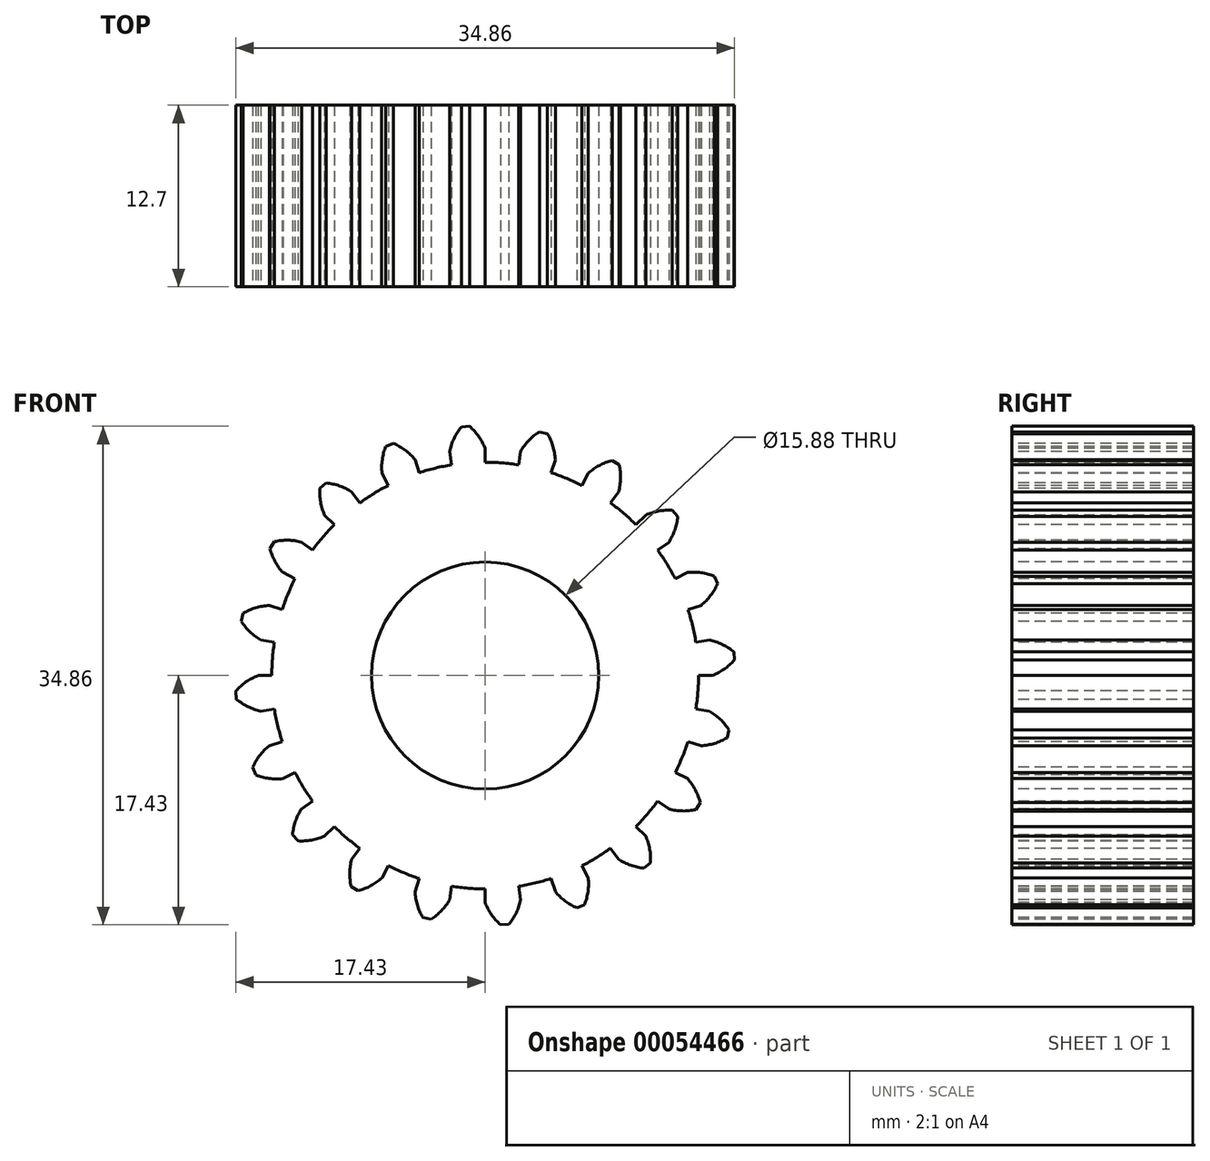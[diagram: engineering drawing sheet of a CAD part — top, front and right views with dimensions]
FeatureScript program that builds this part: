
annotation { "Feature Type Name" : "Feature", "Feature Type Description" : "" }
export const myFeature = defineFeature(function(context is Context, id is Id, definition is map)
    precondition{}
    {
        {
            var Q0;
            Q0=qCreatedBy(makeId("Front.planeOp"),FACE);
            var sketch = newSketch(context, id + "F0", { "sketchPlane" : qUnion([Q0])});
            skArc(sketch, "E0", {"start": v(2.33, 14.73) * mm, "mid": v(1.17, 14.87) * mm, "end": v(0, 14.92) * mm});
            skArc(sketch, "E1", {"start": v(0, 15.88) * mm, "mid": v(-0.45, 16.72) * mm, "end": v(-1.08, 17.43) * mm});
            skLineSegment(sketch, "E2", {"start": v(0, 15.88) * mm, "end": v(0, 14.92) * mm});
            skLineSegment(sketch, "E3.MirrorCS", {"start": v(-2.48, 15.68) * mm, "end": v(-2.33, 14.73) * mm});
            skArc(sketch, "E4.MirrorCS", {"start": v(-2.48, 15.68) * mm, "mid": v(-2.17, 16.58) * mm, "end": v(-1.66, 17.38) * mm});
            skLineSegment(sketch, "E5", {"start": v(-1.66, 17.38) * mm, "end": v(-1.08, 17.43) * mm});
            skLineSegment(sketch, "E6.1.0", {"start": v(-4.9, 15.1) * mm, "end": v(-4.6, 14.19) * mm});
            skArc(sketch, "E6.1.1", {"start": v(-4.9, 15.1) * mm, "mid": v(-5.6, 15.76) * mm, "end": v(-6.41, 16.24) * mm});
            skLineSegment(sketch, "E6.1.2", {"start": v(-6.95, 16.02) * mm, "end": v(-6.41, 16.24) * mm});
            skArc(sketch, "E6.1.3", {"start": v(-7.2, 14.14) * mm, "mid": v(-7.2, 15.1) * mm, "end": v(-6.95, 16.02) * mm});
            skLineSegment(sketch, "E6.1.4", {"start": v(-7.2, 14.14) * mm, "end": v(-6.77, 13.3) * mm});
            skLineSegment(sketch, "E6.2.0", {"start": v(-9.33, 12.84) * mm, "end": v(-8.77, 12.07) * mm});
            skArc(sketch, "E6.2.1", {"start": v(-9.33, 12.84) * mm, "mid": v(-10.19, 13.26) * mm, "end": v(-11.12, 13.46) * mm});
            skLineSegment(sketch, "E6.2.2", {"start": v(-11.56, 13.09) * mm, "end": v(-11.12, 13.46) * mm});
            skArc(sketch, "E6.2.3", {"start": v(-11.23, 11.23) * mm, "mid": v(-11.5, 12.14) * mm, "end": v(-11.56, 13.09) * mm});
            skLineSegment(sketch, "E6.2.4", {"start": v(-11.23, 11.23) * mm, "end": v(-10.55, 10.55) * mm});
            skLineSegment(sketch, "E6.3.0", {"start": v(-12.84, 9.33) * mm, "end": v(-12.07, 8.77) * mm});
            skArc(sketch, "E6.3.1", {"start": v(-12.84, 9.33) * mm, "mid": v(-13.79, 9.46) * mm, "end": v(-14.74, 9.37) * mm});
            skLineSegment(sketch, "E6.3.2", {"start": v(-15.04, 8.88) * mm, "end": v(-14.74, 9.37) * mm});
            skArc(sketch, "E6.3.3", {"start": v(-14.14, 7.2) * mm, "mid": v(-14.7, 7.99) * mm, "end": v(-15.04, 8.88) * mm});
            skLineSegment(sketch, "E6.3.4", {"start": v(-14.14, 7.2) * mm, "end": v(-13.3, 6.77) * mm});
            skLineSegment(sketch, "E6.4.0", {"start": v(-15.1, 4.9) * mm, "end": v(-14.19, 4.6) * mm});
            skArc(sketch, "E6.4.1", {"start": v(-15.1, 4.9) * mm, "mid": v(-16.04, 4.74) * mm, "end": v(-16.91, 4.36) * mm});
            skLineSegment(sketch, "E6.4.2", {"start": v(-17.05, 3.8) * mm, "end": v(-16.91, 4.36) * mm});
            skArc(sketch, "E6.4.3", {"start": v(-15.68, 2.48) * mm, "mid": v(-16.44, 3.06) * mm, "end": v(-17.05, 3.8) * mm});
            skLineSegment(sketch, "E6.4.4", {"start": v(-15.68, 2.48) * mm, "end": v(-14.73, 2.33) * mm});
            skLineSegment(sketch, "E6.5.0", {"start": v(-15.88, 0) * mm, "end": v(-14.92, 0) * mm});
            skArc(sketch, "E6.5.1", {"start": v(-15.88, 0) * mm, "mid": v(-16.72, -0.45) * mm, "end": v(-17.43, -1.08) * mm});
            skLineSegment(sketch, "E6.5.2", {"start": v(-17.38, -1.66) * mm, "end": v(-17.43, -1.08) * mm});
            skArc(sketch, "E6.5.3", {"start": v(-15.68, -2.48) * mm, "mid": v(-16.58, -2.17) * mm, "end": v(-17.38, -1.66) * mm});
            skLineSegment(sketch, "E6.5.4", {"start": v(-15.68, -2.48) * mm, "end": v(-14.73, -2.33) * mm});
            skLineSegment(sketch, "E6.6.0", {"start": v(-15.1, -4.9) * mm, "end": v(-14.19, -4.6) * mm});
            skArc(sketch, "E6.6.1", {"start": v(-15.1, -4.9) * mm, "mid": v(-15.76, -5.6) * mm, "end": v(-16.24, -6.41) * mm});
            skLineSegment(sketch, "E6.6.2", {"start": v(-16.02, -6.95) * mm, "end": v(-16.24, -6.41) * mm});
            skArc(sketch, "E6.6.3", {"start": v(-14.14, -7.2) * mm, "mid": v(-15.1, -7.2) * mm, "end": v(-16.02, -6.95) * mm});
            skLineSegment(sketch, "E6.6.4", {"start": v(-14.14, -7.2) * mm, "end": v(-13.3, -6.77) * mm});
            skLineSegment(sketch, "E6.7.0", {"start": v(-12.84, -9.33) * mm, "end": v(-12.07, -8.77) * mm});
            skArc(sketch, "E6.7.1", {"start": v(-12.84, -9.33) * mm, "mid": v(-13.26, -10.19) * mm, "end": v(-13.46, -11.12) * mm});
            skLineSegment(sketch, "E6.7.2", {"start": v(-13.09, -11.56) * mm, "end": v(-13.46, -11.12) * mm});
            skArc(sketch, "E6.7.3", {"start": v(-11.23, -11.23) * mm, "mid": v(-12.14, -11.5) * mm, "end": v(-13.09, -11.56) * mm});
            skLineSegment(sketch, "E6.7.4", {"start": v(-11.23, -11.23) * mm, "end": v(-10.55, -10.55) * mm});
            skLineSegment(sketch, "E6.8.0", {"start": v(-9.33, -12.84) * mm, "end": v(-8.77, -12.07) * mm});
            skArc(sketch, "E6.8.1", {"start": v(-9.33, -12.84) * mm, "mid": v(-9.46, -13.79) * mm, "end": v(-9.37, -14.74) * mm});
            skLineSegment(sketch, "E6.8.2", {"start": v(-8.88, -15.04) * mm, "end": v(-9.37, -14.74) * mm});
            skArc(sketch, "E6.8.3", {"start": v(-7.2, -14.14) * mm, "mid": v(-7.99, -14.7) * mm, "end": v(-8.88, -15.04) * mm});
            skLineSegment(sketch, "E6.8.4", {"start": v(-7.2, -14.14) * mm, "end": v(-6.77, -13.3) * mm});
            skLineSegment(sketch, "E6.9.0", {"start": v(-4.9, -15.1) * mm, "end": v(-4.6, -14.19) * mm});
            skArc(sketch, "E6.9.1", {"start": v(-4.9, -15.1) * mm, "mid": v(-4.74, -16.04) * mm, "end": v(-4.36, -16.91) * mm});
            skLineSegment(sketch, "E6.9.2", {"start": v(-3.8, -17.05) * mm, "end": v(-4.36, -16.91) * mm});
            skArc(sketch, "E6.9.3", {"start": v(-2.48, -15.68) * mm, "mid": v(-3.06, -16.44) * mm, "end": v(-3.8, -17.05) * mm});
            skLineSegment(sketch, "E6.9.4", {"start": v(-2.48, -15.68) * mm, "end": v(-2.33, -14.73) * mm});
            skLineSegment(sketch, "E6.10.0", {"start": v(0, -15.88) * mm, "end": v(0, -14.92) * mm});
            skArc(sketch, "E6.10.1", {"start": v(0, -15.88) * mm, "mid": v(0.45, -16.72) * mm, "end": v(1.08, -17.43) * mm});
            skLineSegment(sketch, "E6.10.2", {"start": v(1.66, -17.38) * mm, "end": v(1.08, -17.43) * mm});
            skArc(sketch, "E6.10.3", {"start": v(2.48, -15.68) * mm, "mid": v(2.17, -16.58) * mm, "end": v(1.66, -17.38) * mm});
            skLineSegment(sketch, "E6.10.4", {"start": v(2.48, -15.68) * mm, "end": v(2.33, -14.73) * mm});
            skLineSegment(sketch, "E6.11.0", {"start": v(4.9, -15.1) * mm, "end": v(4.6, -14.19) * mm});
            skArc(sketch, "E6.11.1", {"start": v(4.9, -15.1) * mm, "mid": v(5.6, -15.76) * mm, "end": v(6.41, -16.24) * mm});
            skLineSegment(sketch, "E6.11.2", {"start": v(6.95, -16.02) * mm, "end": v(6.41, -16.24) * mm});
            skArc(sketch, "E6.11.3", {"start": v(7.2, -14.14) * mm, "mid": v(7.2, -15.1) * mm, "end": v(6.95, -16.02) * mm});
            skLineSegment(sketch, "E6.11.4", {"start": v(7.2, -14.14) * mm, "end": v(6.77, -13.3) * mm});
            skLineSegment(sketch, "E6.12.0", {"start": v(9.33, -12.84) * mm, "end": v(8.77, -12.07) * mm});
            skArc(sketch, "E6.12.1", {"start": v(9.33, -12.84) * mm, "mid": v(10.19, -13.26) * mm, "end": v(11.12, -13.46) * mm});
            skLineSegment(sketch, "E6.12.2", {"start": v(11.56, -13.09) * mm, "end": v(11.12, -13.46) * mm});
            skArc(sketch, "E6.12.3", {"start": v(11.23, -11.23) * mm, "mid": v(11.5, -12.14) * mm, "end": v(11.56, -13.09) * mm});
            skLineSegment(sketch, "E6.12.4", {"start": v(11.23, -11.23) * mm, "end": v(10.55, -10.55) * mm});
            skLineSegment(sketch, "E6.13.0", {"start": v(12.84, -9.33) * mm, "end": v(12.07, -8.77) * mm});
            skArc(sketch, "E6.13.1", {"start": v(12.84, -9.33) * mm, "mid": v(13.79, -9.46) * mm, "end": v(14.74, -9.37) * mm});
            skLineSegment(sketch, "E6.13.2", {"start": v(15.04, -8.88) * mm, "end": v(14.74, -9.37) * mm});
            skArc(sketch, "E6.13.3", {"start": v(14.14, -7.2) * mm, "mid": v(14.7, -7.99) * mm, "end": v(15.04, -8.88) * mm});
            skLineSegment(sketch, "E6.13.4", {"start": v(14.14, -7.2) * mm, "end": v(13.3, -6.77) * mm});
            skLineSegment(sketch, "E6.14.0", {"start": v(15.1, -4.9) * mm, "end": v(14.19, -4.6) * mm});
            skArc(sketch, "E6.14.1", {"start": v(15.1, -4.9) * mm, "mid": v(16.04, -4.74) * mm, "end": v(16.91, -4.36) * mm});
            skLineSegment(sketch, "E6.14.2", {"start": v(17.05, -3.8) * mm, "end": v(16.91, -4.36) * mm});
            skArc(sketch, "E6.14.3", {"start": v(15.68, -2.48) * mm, "mid": v(16.44, -3.06) * mm, "end": v(17.05, -3.8) * mm});
            skLineSegment(sketch, "E6.14.4", {"start": v(15.68, -2.48) * mm, "end": v(14.73, -2.33) * mm});
            skLineSegment(sketch, "E6.15.0", {"start": v(15.88, 0) * mm, "end": v(14.92, 0) * mm});
            skArc(sketch, "E6.15.1", {"start": v(15.88, 0) * mm, "mid": v(16.72, 0.45) * mm, "end": v(17.43, 1.08) * mm});
            skLineSegment(sketch, "E6.15.2", {"start": v(17.38, 1.66) * mm, "end": v(17.43, 1.08) * mm});
            skArc(sketch, "E6.15.3", {"start": v(15.68, 2.48) * mm, "mid": v(16.58, 2.17) * mm, "end": v(17.38, 1.66) * mm});
            skLineSegment(sketch, "E6.15.4", {"start": v(15.68, 2.48) * mm, "end": v(14.73, 2.33) * mm});
            skLineSegment(sketch, "E6.16.0", {"start": v(15.1, 4.9) * mm, "end": v(14.19, 4.6) * mm});
            skArc(sketch, "E6.16.1", {"start": v(15.1, 4.9) * mm, "mid": v(15.76, 5.6) * mm, "end": v(16.24, 6.41) * mm});
            skLineSegment(sketch, "E6.16.2", {"start": v(16.02, 6.95) * mm, "end": v(16.24, 6.41) * mm});
            skArc(sketch, "E6.16.3", {"start": v(14.14, 7.2) * mm, "mid": v(15.1, 7.2) * mm, "end": v(16.02, 6.95) * mm});
            skLineSegment(sketch, "E6.16.4", {"start": v(14.14, 7.2) * mm, "end": v(13.3, 6.77) * mm});
            skLineSegment(sketch, "E6.17.0", {"start": v(12.84, 9.33) * mm, "end": v(12.07, 8.77) * mm});
            skArc(sketch, "E6.17.1", {"start": v(12.84, 9.33) * mm, "mid": v(13.26, 10.19) * mm, "end": v(13.46, 11.12) * mm});
            skLineSegment(sketch, "E6.17.2", {"start": v(13.09, 11.56) * mm, "end": v(13.46, 11.12) * mm});
            skArc(sketch, "E6.17.3", {"start": v(11.23, 11.23) * mm, "mid": v(12.14, 11.5) * mm, "end": v(13.09, 11.56) * mm});
            skLineSegment(sketch, "E6.17.4", {"start": v(11.23, 11.23) * mm, "end": v(10.55, 10.55) * mm});
            skLineSegment(sketch, "E6.18.0", {"start": v(9.33, 12.84) * mm, "end": v(8.77, 12.07) * mm});
            skArc(sketch, "E6.18.1", {"start": v(9.33, 12.84) * mm, "mid": v(9.46, 13.79) * mm, "end": v(9.37, 14.74) * mm});
            skLineSegment(sketch, "E6.18.2", {"start": v(8.88, 15.04) * mm, "end": v(9.37, 14.74) * mm});
            skArc(sketch, "E6.18.3", {"start": v(7.2, 14.14) * mm, "mid": v(7.99, 14.7) * mm, "end": v(8.88, 15.04) * mm});
            skLineSegment(sketch, "E6.18.4", {"start": v(7.2, 14.14) * mm, "end": v(6.77, 13.3) * mm});
            skLineSegment(sketch, "E6.19.0", {"start": v(4.9, 15.1) * mm, "end": v(4.6, 14.19) * mm});
            skArc(sketch, "E6.19.1", {"start": v(4.9, 15.1) * mm, "mid": v(4.74, 16.04) * mm, "end": v(4.36, 16.91) * mm});
            skLineSegment(sketch, "E6.19.2", {"start": v(3.8, 17.05) * mm, "end": v(4.36, 16.91) * mm});
            skArc(sketch, "E6.19.3", {"start": v(2.48, 15.68) * mm, "mid": v(3.06, 16.44) * mm, "end": v(3.8, 17.05) * mm});
            skLineSegment(sketch, "E6.19.4", {"start": v(2.48, 15.68) * mm, "end": v(2.33, 14.73) * mm});
            skArc(sketch, "E7.trimOffspring", {"start": v(6.77, 13.3) * mm, "mid": v(5.7, 13.78) * mm, "end": v(4.6, 14.19) * mm});
            skArc(sketch, "E8.trimOffspring", {"start": v(10.55, 10.55) * mm, "mid": v(9.69, 11.34) * mm, "end": v(8.77, 12.07) * mm});
            skArc(sketch, "E9.trimOffspring", {"start": v(13.3, 6.77) * mm, "mid": v(12.72, 7.8) * mm, "end": v(12.07, 8.77) * mm});
            skArc(sketch, "E10.trimOffspring", {"start": v(14.73, 2.33) * mm, "mid": v(14.5, 3.48) * mm, "end": v(14.19, 4.6) * mm});
            skArc(sketch, "E11.trimOffspring", {"start": v(14.73, -2.33) * mm, "mid": v(14.87, -1.17) * mm, "end": v(14.92, 0) * mm});
            skArc(sketch, "E12.trimOffspring", {"start": v(13.3, -6.77) * mm, "mid": v(13.78, -5.7) * mm, "end": v(14.19, -4.6) * mm});
            skArc(sketch, "E13.trimOffspring", {"start": v(10.55, -10.55) * mm, "mid": v(11.34, -9.69) * mm, "end": v(12.07, -8.77) * mm});
            skArc(sketch, "E14.trimOffspring", {"start": v(6.77, -13.3) * mm, "mid": v(7.8, -12.72) * mm, "end": v(8.77, -12.07) * mm});
            skArc(sketch, "E15.trimOffspring", {"start": v(2.33, -14.73) * mm, "mid": v(3.48, -14.5) * mm, "end": v(4.6, -14.19) * mm});
            skArc(sketch, "E16.trimOffspring", {"start": v(-2.33, -14.73) * mm, "mid": v(-1.17, -14.87) * mm, "end": v(0, -14.92) * mm});
            skArc(sketch, "E17.trimOffspring", {"start": v(-6.77, -13.3) * mm, "mid": v(-5.7, -13.78) * mm, "end": v(-4.6, -14.19) * mm});
            skArc(sketch, "E18.trimOffspring", {"start": v(-10.55, -10.55) * mm, "mid": v(-9.69, -11.34) * mm, "end": v(-8.77, -12.07) * mm});
            skArc(sketch, "E19.trimOffspring", {"start": v(-13.3, -6.77) * mm, "mid": v(-12.72, -7.8) * mm, "end": v(-12.07, -8.77) * mm});
            skArc(sketch, "E20.trimOffspring", {"start": v(-14.73, -2.33) * mm, "mid": v(-14.5, -3.48) * mm, "end": v(-14.19, -4.6) * mm});
            skArc(sketch, "E21.trimOffspring", {"start": v(-14.73, 2.33) * mm, "mid": v(-14.87, 1.17) * mm, "end": v(-14.92, 0) * mm});
            skArc(sketch, "E22.trimOffspring", {"start": v(-13.3, 6.77) * mm, "mid": v(-13.78, 5.7) * mm, "end": v(-14.19, 4.6) * mm});
            skArc(sketch, "E23.trimOffspring", {"start": v(-10.55, 10.55) * mm, "mid": v(-11.34, 9.69) * mm, "end": v(-12.07, 8.77) * mm});
            skArc(sketch, "E24.trimOffspring", {"start": v(-6.77, 13.3) * mm, "mid": v(-7.8, 12.72) * mm, "end": v(-8.77, 12.07) * mm});
            skArc(sketch, "E25.trimOffspring", {"start": v(-2.33, 14.73) * mm, "mid": v(-2.8, 14.65) * mm, "end": v(-3.26, 14.56) * mm});
            skArc(sketch, "E26.trimOffspring", {"start": v(-3.7, 14.45) * mm, "mid": v(-4.16, 14.33) * mm, "end": v(-4.6, 14.19) * mm});
            skArc(sketch, "E27", {"start": v(-3.26, 14.56) * mm, "mid": v(-3.48, 14.5) * mm, "end": v(-3.7, 14.45) * mm});
            skCircle(sketch, "E28", {"center": v(0, 0) * mm, "radius": 7.94 * mm});
            skSolve(sketch);
        }
        {
            var Q0;
            Q0 = qSketchRegion(id + "F0", true);
            var Q1;
            Q1=makeQuery(id+"F0.imprint","IMPRINT",FACE,{"disambiguationData":[TD([[makeQuery(id+"F0.imprint","IMPRINT",EDGE,{"derivedFrom":sQuery(id+"F0.wireOp",EDGE,"E0")}),1.0]])]});
            extrude(context, id + "F1", {"entities" : qUnion([Q0, Q1]), "oppositeDirection" : true, "depth" : 12.7 * mm});
        }
    });
